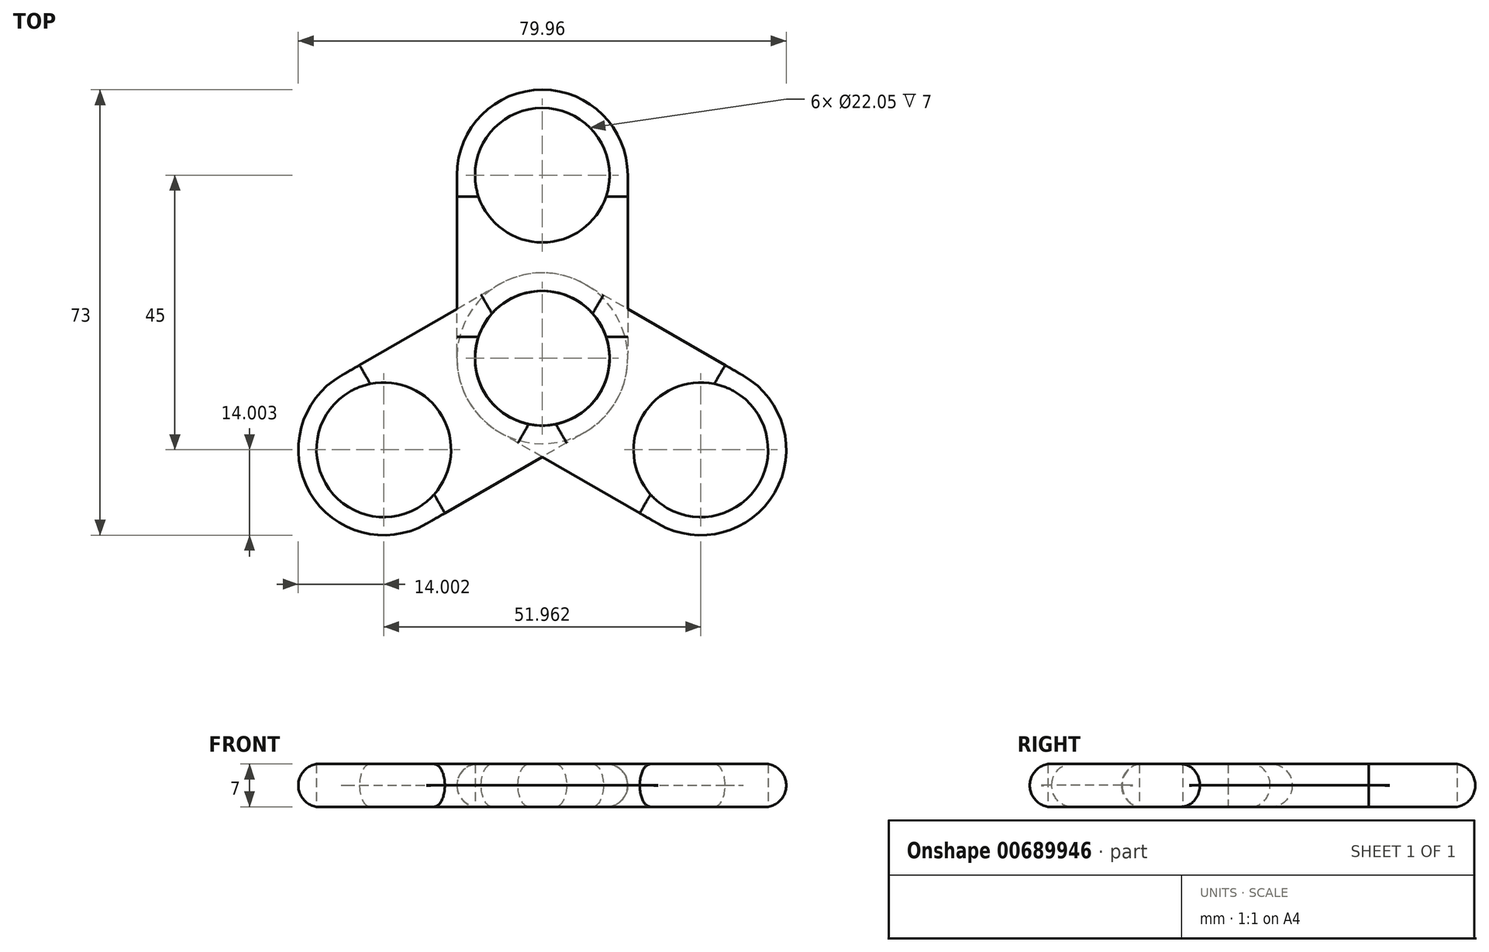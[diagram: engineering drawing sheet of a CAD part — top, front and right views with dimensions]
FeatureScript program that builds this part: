
annotation { "Feature Type Name" : "Feature", "Feature Type Description" : "" }
export const myFeature = defineFeature(function(context is Context, id is Id, definition is map)
    precondition{}
    {
        {
            var Q0;
            Q0=qCreatedBy(makeId("Top.planeOp"),FACE);
            var sketch = newSketch(context, id + "F0", { "sketchPlane" : qUnion([Q0])});
            skLineSegment(sketch, "E0.bottom", {"start": v(-36.69, -0.56) * mm, "end": v(-8.69, -0.56) * mm});
            skLineSegment(sketch, "E0.top", {"start": v(-36.69, -30.56) * mm, "end": v(-8.69, -30.56) * mm});
            skLineSegment(sketch, "E0.left", {"start": v(-36.69, -0.56) * mm, "end": v(-36.69, -30.56) * mm});
            skLineSegment(sketch, "E0.right", {"start": v(-8.69, -0.56) * mm, "end": v(-8.69, -30.56) * mm});
            skCircle(sketch, "E1", {"center": v(-22.69, -0.56) * mm, "radius": 14 * mm});
            skCircle(sketch, "E2", {"center": v(-22.69, -0.56) * mm, "radius": 11.03 * mm});
            skCircle(sketch, "E3", {"center": v(-22.69, -30.56) * mm, "radius": 14 * mm});
            skCircle(sketch, "E4", {"center": v(-22.69, -30.56) * mm, "radius": 11.03 * mm});
            skSolve(sketch);
        }
        {
            var Q0;
            {var subQ1=sQuery(id+"F0.wireOp",EDGE,"E0.bottom");var subQ3=sQuery(id+"F0.wireOp",EDGE,"E2");var subQ4=makeQuery(id+"F0.imprint","INTERSECT",VERTEX,{"disambiguationData":[OD(0.0)],"derivedFrom":[subQ1,subQ3]});Q0=makeQuery(id+"F0.imprint","IMPRINT",FACE,{"disambiguationData":[TD([[makeQuery(id+"F0.imprint","IMPRINT",EDGE,{"disambiguationData":[TD([[subQ4,1.0]])],"derivedFrom":subQ3}),-1.0]])]});}
            var Q1;
            {var subQ1=sQuery(id+"F0.wireOp",EDGE,"E0.bottom");var subQ3=sQuery(id+"F0.wireOp",EDGE,"E2");var subQ4=makeQuery(id+"F0.imprint","INTERSECT",VERTEX,{"disambiguationData":[OD(0.0)],"derivedFrom":[subQ1,subQ3]});Q1=makeQuery(id+"F0.imprint","IMPRINT",FACE,{"disambiguationData":[TD([[makeQuery(id+"F0.imprint","IMPRINT",EDGE,{"disambiguationData":[TD([[subQ4,-1.0]])],"derivedFrom":subQ3}),-1.0]])]});}
            var Q2;
            {var subQ0=sQuery(id+"F0.wireOp",EDGE,"E0.left");Q2=makeQuery(id+"F0.imprint","IMPRINT",FACE,{"disambiguationData":[TD([[makeQuery(id+"F0.imprint","IMPRINT",EDGE,{"derivedFrom":subQ0}),1.0]])]});}
            var Q3;
            {var subQ1=sQuery(id+"F0.wireOp",EDGE,"E0.top");var subQ3=sQuery(id+"F0.wireOp",EDGE,"E4");var subQ4=makeQuery(id+"F0.imprint","INTERSECT",VERTEX,{"disambiguationData":[OD(0.0)],"derivedFrom":[subQ1,subQ3]});Q3=makeQuery(id+"F0.imprint","IMPRINT",FACE,{"disambiguationData":[TD([[makeQuery(id+"F0.imprint","IMPRINT",EDGE,{"disambiguationData":[TD([[subQ4,1.0]])],"derivedFrom":subQ3}),-1.0]])]});}
            var Q4;
            {var subQ1=sQuery(id+"F0.wireOp",EDGE,"E0.top");var subQ3=sQuery(id+"F0.wireOp",EDGE,"E4");var subQ4=makeQuery(id+"F0.imprint","INTERSECT",VERTEX,{"disambiguationData":[OD(0.0)],"derivedFrom":[subQ1,subQ3]});Q4=makeQuery(id+"F0.imprint","IMPRINT",FACE,{"disambiguationData":[TD([[makeQuery(id+"F0.imprint","IMPRINT",EDGE,{"disambiguationData":[TD([[subQ4,-1.0]])],"derivedFrom":subQ3}),-1.0]])]});}
            extrude(context, id + "F1", {"entities" : qUnion([Q0, Q1, Q2, Q3, Q4]), "depth" : 7 * mm, "offsetDistance" : 25 * mm});
        }
        {
            var Q0;
            Q0=makeQuery(id+"F1.opExtrude","CAP_EDGE",EDGE,{"disambiguationData":[OSD([sQuery(id+"F0.wireOp",EDGE,"E0.left")])],"isStart":false});
            var Q1;
            Q1=makeQuery(id+"F1.opExtrude","CAP_EDGE",EDGE,{"disambiguationData":[OSD([sQuery(id+"F0.wireOp",EDGE,"E3")])],"isStart":false});
            var Q2;
            Q2=makeQuery(id+"F1.opExtrude","CAP_EDGE",EDGE,{"disambiguationData":[OSD([sQuery(id+"F0.wireOp",EDGE,"E0.right")])],"isStart":false});
            var Q3;
            Q3=makeQuery(id+"F1.opExtrude","CAP_EDGE",EDGE,{"disambiguationData":[OSD([sQuery(id+"F0.wireOp",EDGE,"E1")])],"isStart":false});
            var Q4;
            Q4=makeQuery(id+"F1.opExtrude","CAP_EDGE",EDGE,{"disambiguationData":[OSD([sQuery(id+"F0.wireOp",EDGE,"E1")])],"isStart":true});
            var Q5;
            Q5=makeQuery(id+"F1.opExtrude","CAP_EDGE",EDGE,{"disambiguationData":[OSD([sQuery(id+"F0.wireOp",EDGE,"E0.right")])],"isStart":true});
            var Q6;
            Q6=makeQuery(id+"F1.opExtrude","CAP_EDGE",EDGE,{"disambiguationData":[OSD([sQuery(id+"F0.wireOp",EDGE,"E0.left")])],"isStart":true});
            var Q7;
            Q7=makeQuery(id+"F1.opExtrude","CAP_EDGE",EDGE,{"disambiguationData":[OSD([sQuery(id+"F0.wireOp",EDGE,"E3")])],"isStart":true});
            fillet(context, id + "F2", {"entities" : qUnion([Q0, Q1, Q2, Q3, Q4, Q5, Q6, Q7]), "radius" : 3.54 * mm, "tangentPropagation" : true, "allowEdgeOverflow" : false});
        }
        {
            var Q0;
            Q0=makeQuery(id+"F1.opExtrude","SWEPT_BODY",BODY,{"disambiguationData":[OSD([sQuery(id+"F0.wireOp",EDGE,"E0.left"),sQuery(id+"F0.wireOp",EDGE,"E0.right"),sQuery(id+"F0.wireOp",EDGE,"E1"),sQuery(id+"F0.wireOp",EDGE,"E2"),sQuery(id+"F0.wireOp",EDGE,"E3"),sQuery(id+"F0.wireOp",EDGE,"E4")])]});
            var Q1;
            {var subQ0=sQuery(id+"F0.wireOp",EDGE,"E0.right");Q1=makeQuery(id+"F2.opFillet","BLEND_FACE",FACE,{"disambiguationData":[OSD([subQ0]),TDD([makeQuery(id+"F1.opExtrude","CAP_EDGE",EDGE,{"disambiguationData":[OSD([subQ0])],"isStart":false})]),OD(0.0)]});}
            circularPattern(context, id + "F3", {"entities" : qUnion([Q0]), "axis" : qUnion([Q1]), "angle" : 360 * degree, "instanceCount" : 3, "equalSpace" : true});
        }
    });
